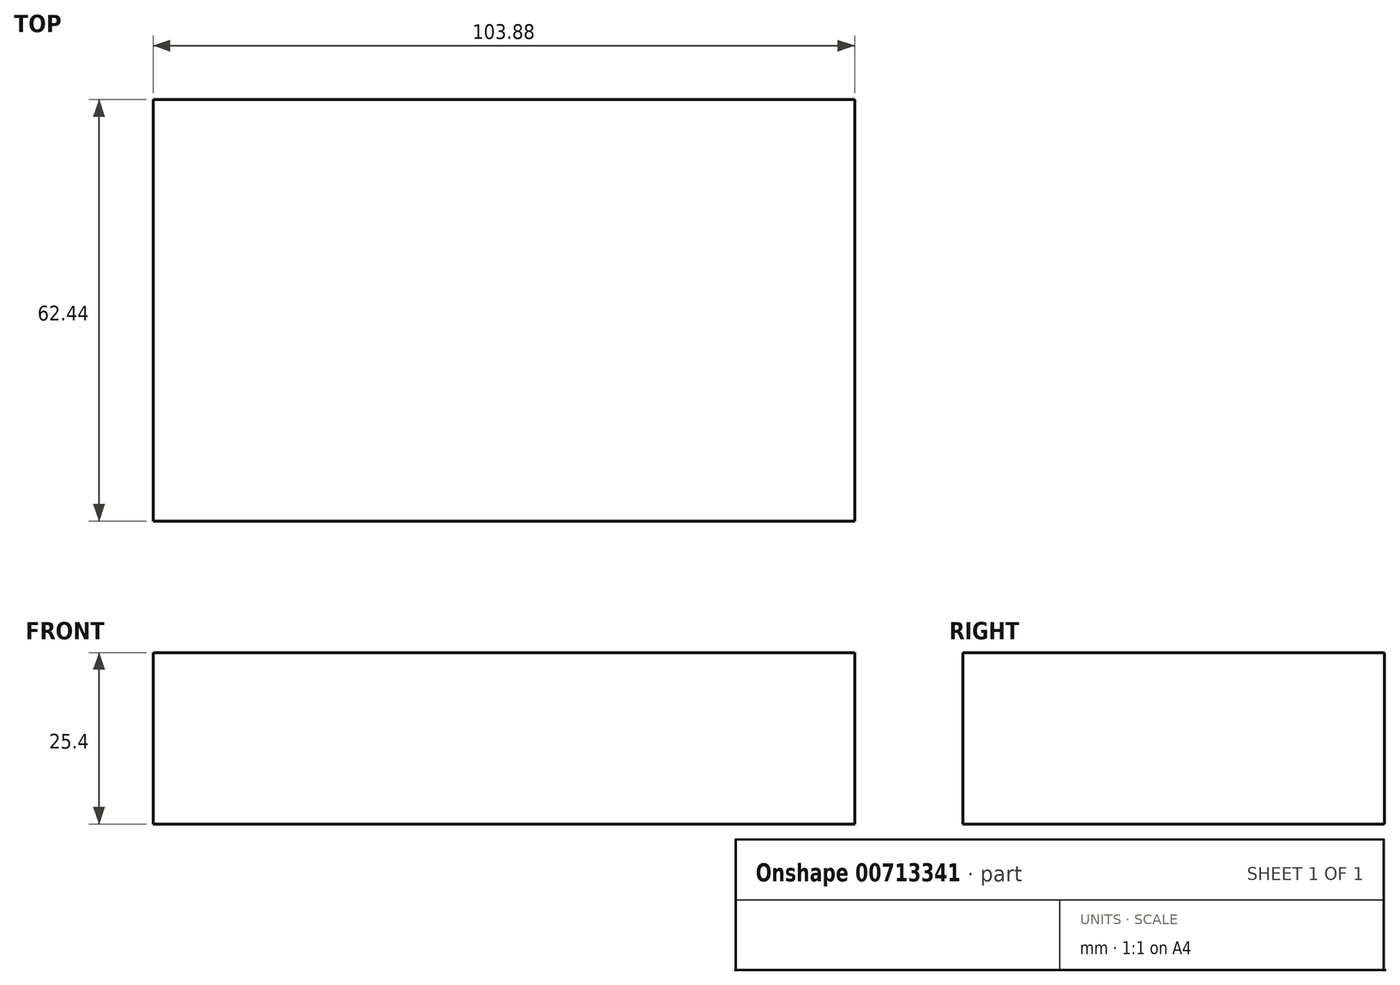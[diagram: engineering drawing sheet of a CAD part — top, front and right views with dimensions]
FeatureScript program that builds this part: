
annotation { "Feature Type Name" : "Feature", "Feature Type Description" : "" }
export const myFeature = defineFeature(function(context is Context, id is Id, definition is map)
    precondition{}
    {
        {
            var Q0;
            Q0=qCreatedBy(makeId("Top.planeOp"),FACE);
            var sketch = newSketch(context, id + "F0", { "sketchPlane" : qUnion([Q0])});
            skLineSegment(sketch, "E0.bottom", {"start": v(-46.9, 29.45) * mm, "end": v(57, 29.45) * mm});
            skLineSegment(sketch, "E0.top", {"start": v(-46.9, -32.99) * mm, "end": v(57, -32.99) * mm});
            skLineSegment(sketch, "E0.left", {"start": v(-46.9, 29.45) * mm, "end": v(-46.9, -32.99) * mm});
            skLineSegment(sketch, "E0.right", {"start": v(57, 29.45) * mm, "end": v(57, -32.99) * mm});
            skSolve(sketch);
        }
        {
            var Q0;
            Q0 = qSketchRegion(id + "F0", true);
            extrude(context, id + "F1", {"entities" : qUnion([Q0]), "depth" : 25.4 * mm, "offsetDistance" : 25.4 * mm});
        }
    });
